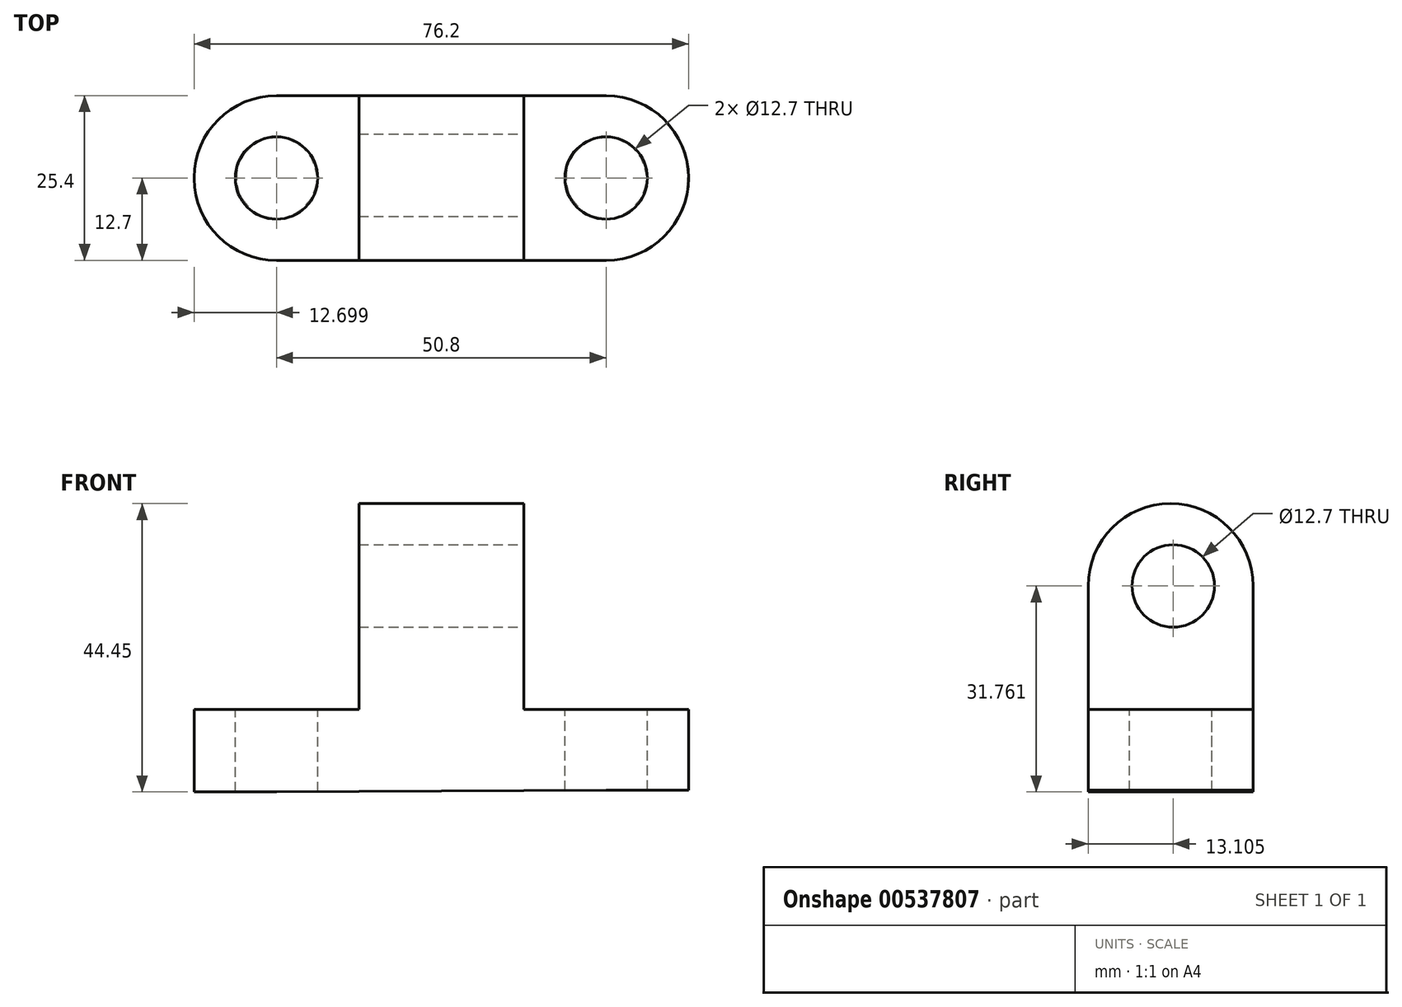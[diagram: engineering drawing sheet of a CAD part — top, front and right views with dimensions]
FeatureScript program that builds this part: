
annotation { "Feature Type Name" : "Feature", "Feature Type Description" : "" }
export const myFeature = defineFeature(function(context is Context, id is Id, definition is map)
    precondition{}
    {
        {
            var Q0;
            Q0=qCreatedBy(makeId("Front.planeOp"),FACE);
            var sketch = newSketch(context, id + "F0", { "sketchPlane" : qUnion([Q0])});
            skLineSegment(sketch, "E0", {"start": v(-31.75, -0.3) * mm, "end": v(-31.75, 12.4) * mm});
            skLineSegment(sketch, "E1", {"start": v(-31.75, 12.4) * mm, "end": v(-6.35, 12.4) * mm});
            skLineSegment(sketch, "E2", {"start": v(-6.35, 44.15) * mm, "end": v(19.05, 44.15) * mm});
            skLineSegment(sketch, "E3", {"start": v(19.05, 44.15) * mm, "end": v(19.05, 12.4) * mm});
            skLineSegment(sketch, "E4", {"start": v(19.05, 12.4) * mm, "end": v(44.45, 12.4) * mm});
            skLineSegment(sketch, "E5", {"start": v(44.45, 12.4) * mm, "end": v(44.45, 0) * mm});
            skLineSegment(sketch, "E6", {"start": v(-6.35, 12.4) * mm, "end": v(-6.35, 44.15) * mm});
            skPoint(sketch, "E7.end.orphan", {"position": v(-38.1, 0) * mm});
            skLineSegment(sketch, "E8", {"start": v(-31.75, -0.3) * mm, "end": v(44.45, 0) * mm});
            skSolve(sketch);
        }
        {
            var Q0;
            Q0=makeQuery(id+"F0.imprint","IMPRINT",FACE,{"disambiguationData":[TD([[makeQuery(id+"F0.imprint","IMPRINT",EDGE,{"derivedFrom":sQuery(id+"F0.wireOp",EDGE,"E0")}),-1.0]])]});
            extrude(context, id + "F1", {"entities" : qUnion([Q0]), "depth" : 25.4 * mm, "offsetDistance" : 25.4 * mm});
        }
        {
            var Q0;
            Q0=makeQuery(id+"F1.opExtrude","SWEPT_FACE",FACE,{"disambiguationData":[OSD([sQuery(id+"F0.wireOp",EDGE,"E1")])]});
            var sketch = newSketch(context, id + "F2", { "sketchPlane" : qUnion([Q0])});
            skCircle(sketch, "E9", {"center": v(-19.05, -12.7) * mm, "radius": 6.35 * mm});
            skArc(sketch, "E10", {"start": v(-19.05, 0) * mm, "mid": v(-31.75, -12.7) * mm, "end": v(-19.05, -25.4) * mm});
            skSolve(sketch);
        }
        {
            var Q0;
            Q0=makeQuery(id+"F2.imprint","IMPRINT",FACE,{"disambiguationData":[TD([[makeQuery(id+"F2.imprint","IMPRINT",EDGE,{"derivedFrom":sQuery(id+"F2.wireOp",EDGE,"E9")}),1.0]])]});
            var Q1;
            {var subQ0=sQuery(id+"F2.wireOp",EDGE,"E10");var subQ1=sQuery(id+"F0.wireOp",EDGE,"E1");var subQ2=makeQuery(id+"F1.opExtrude","CAP_EDGE",EDGE,{"disambiguationData":[OSD([subQ1])],"isStart":true});var subQ3=makeQuery(id+"F2.imprint","INTERSECT",VERTEX,{"derivedFrom":[subQ2,subQ0]});Q1=makeQuery(id+"F2.imprint","IMPRINT",FACE,{"disambiguationData":[TD([[makeQuery(id+"F2.imprint","IMPRINT",EDGE,{"disambiguationData":[TD([[subQ3,-1.0]])],"derivedFrom":subQ0}),-1.0]])]});}
            var Q2;
            {var subQ0=sQuery(id+"F2.wireOp",EDGE,"E10");var subQ1=sQuery(id+"F0.wireOp",EDGE,"E1");var subQ2=makeQuery(id+"F1.opExtrude","CAP_EDGE",EDGE,{"disambiguationData":[OSD([subQ1])],"isStart":false});var subQ3=makeQuery(id+"F2.imprint","INTERSECT",VERTEX,{"derivedFrom":[subQ2,subQ0]});Q2=makeQuery(id+"F2.imprint","IMPRINT",FACE,{"disambiguationData":[TD([[makeQuery(id+"F2.imprint","IMPRINT",EDGE,{"disambiguationData":[TD([[subQ3,1.0]])],"derivedFrom":subQ0}),-1.0]])]});}
            extrude(context, id + "F3", {"entities" : qUnion([Q0, Q1, Q2]), "operationType" : NewBodyOperationType.REMOVE, "oppositeDirection" : true, "depth" : 25.4 * mm, "offsetDistance" : 25.4 * mm});
        }
        {
            var Q0;
            Q0=makeQuery(id+"F1.opExtrude","SWEPT_FACE",FACE,{"disambiguationData":[OSD([sQuery(id+"F0.wireOp",EDGE,"E4")])]});
            var sketch = newSketch(context, id + "F4", { "sketchPlane" : qUnion([Q0])});
            skCircle(sketch, "E11", {"center": v(31.75, -12.7) * mm, "radius": 6.35 * mm});
            skArc(sketch, "E12", {"start": v(31.75, -25.4) * mm, "mid": v(44.45, -12.7) * mm, "end": v(31.75, 0) * mm});
            skSolve(sketch);
        }
        {
            var Q0;
            Q0=makeQuery(id+"F4.imprint","IMPRINT",FACE,{"disambiguationData":[TD([[makeQuery(id+"F4.imprint","IMPRINT",EDGE,{"derivedFrom":sQuery(id+"F4.wireOp",EDGE,"E11")}),1.0]])]});
            var Q1;
            {var subQ0=sQuery(id+"F4.wireOp",EDGE,"E12");var subQ1=sQuery(id+"F0.wireOp",EDGE,"E4");var subQ2=makeQuery(id+"F1.opExtrude","CAP_EDGE",EDGE,{"disambiguationData":[OSD([subQ1])],"isStart":true});var subQ3=makeQuery(id+"F4.imprint","INTERSECT",VERTEX,{"derivedFrom":[subQ2,subQ0]});Q1=makeQuery(id+"F4.imprint","IMPRINT",FACE,{"disambiguationData":[TD([[makeQuery(id+"F4.imprint","IMPRINT",EDGE,{"disambiguationData":[TD([[subQ3,1.0]])],"derivedFrom":subQ0}),-1.0]])]});}
            var Q2;
            {var subQ0=sQuery(id+"F4.wireOp",EDGE,"E12");var subQ1=sQuery(id+"F0.wireOp",EDGE,"E4");var subQ2=makeQuery(id+"F1.opExtrude","CAP_EDGE",EDGE,{"disambiguationData":[OSD([subQ1])],"isStart":false});var subQ3=makeQuery(id+"F4.imprint","INTERSECT",VERTEX,{"derivedFrom":[subQ2,subQ0]});Q2=makeQuery(id+"F4.imprint","IMPRINT",FACE,{"disambiguationData":[TD([[makeQuery(id+"F4.imprint","IMPRINT",EDGE,{"disambiguationData":[TD([[subQ3,-1.0]])],"derivedFrom":subQ0}),-1.0]])]});}
            extrude(context, id + "F5", {"entities" : qUnion([Q0, Q1, Q2]), "operationType" : NewBodyOperationType.REMOVE, "oppositeDirection" : true, "depth" : 25.4 * mm, "offsetDistance" : 25.4 * mm});
        }
        {
            var Q0;
            Q0=makeQuery(id+"F1.opExtrude","SWEPT_FACE",FACE,{"disambiguationData":[OSD([sQuery(id+"F0.wireOp",EDGE,"E3")])]});
            var sketch = newSketch(context, id + "F6", { "sketchPlane" : qUnion([Q0])});
            skCircle(sketch, "E13", {"center": v(-12.3, 31.46) * mm, "radius": 6.35 * mm});
            skArc(sketch, "E14", {"start": v(0, 31.45) * mm, "mid": v(-12.7, 44.15) * mm, "end": v(-25.4, 31.45) * mm});
            skSolve(sketch);
        }
        {
            var Q0;
            Q0=makeQuery(id+"F6.imprint","IMPRINT",FACE,{"disambiguationData":[TD([[makeQuery(id+"F6.imprint","IMPRINT",EDGE,{"derivedFrom":sQuery(id+"F6.wireOp",EDGE,"E13")}),1.0]])]});
            var Q1;
            {var subQ0=sQuery(id+"F6.wireOp",EDGE,"E14");var subQ1=sQuery(id+"F0.wireOp",EDGE,"E3");var subQ2=makeQuery(id+"F1.opExtrude","CAP_EDGE",EDGE,{"disambiguationData":[OSD([subQ1])],"isStart":true});var subQ3=makeQuery(id+"F6.imprint","INTERSECT",VERTEX,{"derivedFrom":[subQ2,subQ0]});Q1=makeQuery(id+"F6.imprint","IMPRINT",FACE,{"disambiguationData":[TD([[makeQuery(id+"F6.imprint","IMPRINT",EDGE,{"disambiguationData":[TD([[subQ3,-1.0]])],"derivedFrom":subQ0}),-1.0]])]});}
            var Q2;
            {var subQ0=sQuery(id+"F6.wireOp",EDGE,"E14");var subQ1=sQuery(id+"F0.wireOp",EDGE,"E3");var subQ2=makeQuery(id+"F1.opExtrude","CAP_EDGE",EDGE,{"disambiguationData":[OSD([subQ1])],"isStart":false});var subQ3=makeQuery(id+"F6.imprint","INTERSECT",VERTEX,{"derivedFrom":[subQ2,subQ0]});Q2=makeQuery(id+"F6.imprint","IMPRINT",FACE,{"disambiguationData":[TD([[makeQuery(id+"F6.imprint","IMPRINT",EDGE,{"disambiguationData":[TD([[subQ3,1.0]])],"derivedFrom":subQ0}),-1.0]])]});}
            extrude(context, id + "F7", {"entities" : qUnion([Q0, Q1, Q2]), "operationType" : NewBodyOperationType.REMOVE, "oppositeDirection" : true, "depth" : 25.4 * mm, "offsetDistance" : 25.4 * mm});
        }
    });
